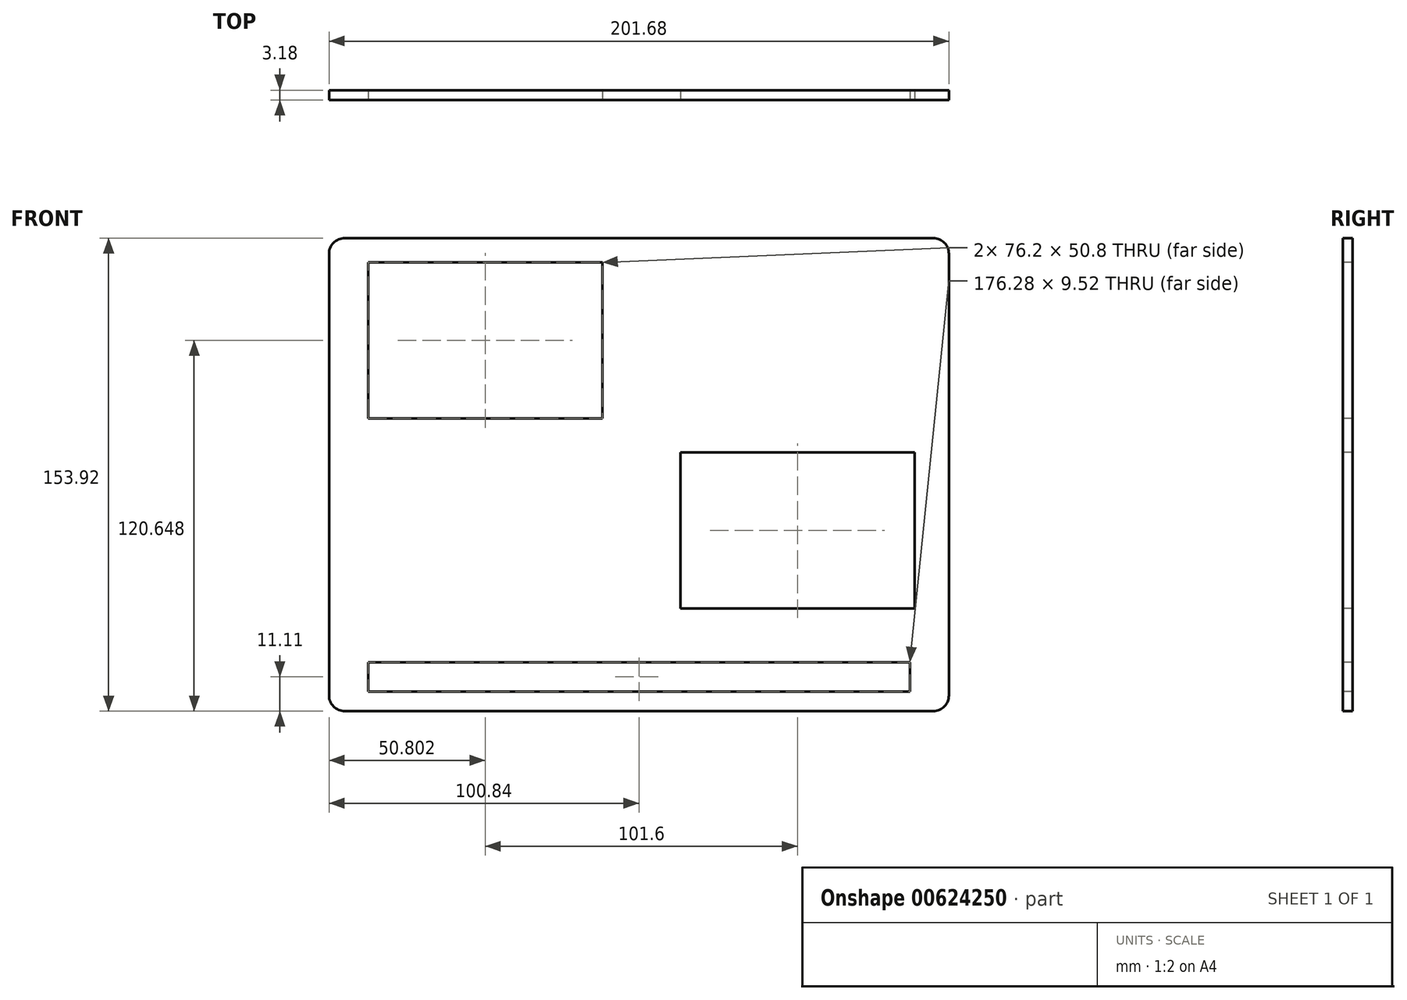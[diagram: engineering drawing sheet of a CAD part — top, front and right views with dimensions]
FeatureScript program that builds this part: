
annotation { "Feature Type Name" : "Feature", "Feature Type Description" : "" }
export const myFeature = defineFeature(function(context is Context, id is Id, definition is map)
    precondition{}
    {
        {
            var Q0;
            Q0=qCreatedBy(makeId("Front.planeOp"),FACE);
            var sketch = newSketch(context, id + "F0", { "sketchPlane" : qUnion([Q0])});
            skLineSegment(sketch, "E0.bottom", {"start": v(-100.84, 76.96) * mm, "end": v(100.84, 76.96) * mm});
            skLineSegment(sketch, "E0.top", {"start": v(-100.84, -76.96) * mm, "end": v(100.84, -76.96) * mm});
            skLineSegment(sketch, "E0.left", {"start": v(-100.84, 76.96) * mm, "end": v(-100.84, -76.96) * mm});
            skLineSegment(sketch, "E0.right", {"start": v(100.84, 76.96) * mm, "end": v(100.84, -76.96) * mm});
            skPoint(sketch, "E0.middle", {"position": v(0, 0) * mm});
            skSolve(sketch);
        }
        {
            var Q0;
            Q0=qSketchRegion(id+"F0",true);
            extrude(context, id + "F1", {"entities" : qUnion([Q0]), "depth" : 3.17 * mm, "offsetDistance" : 25.4 * mm});
        }
        {
            var Q0;
            Q0=makeQuery(id+"F1.opExtrude","CAP_FACE",FACE,{"disambiguationData":[OSD([sQuery(id+"F0.wireOp",EDGE,"E0.bottom"),sQuery(id+"F0.wireOp",EDGE,"E0.top"),sQuery(id+"F0.wireOp",EDGE,"E0.left"),sQuery(id+"F0.wireOp",EDGE,"E0.right")])],"isStart":false});
            var sketch = newSketch(context, id + "F2", { "sketchPlane" : qUnion([Q0])});
            skLineSegment(sketch, "E1.bottom", {"start": v(-88.14, 69.09) * mm, "end": v(-11.94, 69.09) * mm});
            skLineSegment(sketch, "E1.top", {"start": v(-88.14, 18.29) * mm, "end": v(-11.94, 18.29) * mm});
            skLineSegment(sketch, "E1.left", {"start": v(-88.14, 69.09) * mm, "end": v(-88.14, 18.29) * mm});
            skLineSegment(sketch, "E1.right", {"start": v(-11.94, 69.09) * mm, "end": v(-11.94, 18.29) * mm});
            skLineSegment(sketch, "E2.bottom", {"start": v(13.46, 7.18) * mm, "end": v(89.66, 7.18) * mm});
            skLineSegment(sketch, "E2.top", {"start": v(13.46, -43.62) * mm, "end": v(89.66, -43.62) * mm});
            skLineSegment(sketch, "E2.left", {"start": v(13.46, 7.18) * mm, "end": v(13.46, -43.62) * mm});
            skLineSegment(sketch, "E2.right", {"start": v(89.66, 7.18) * mm, "end": v(89.66, -43.62) * mm});
            skSolve(sketch);
        }
        {
            var Q0;
            Q0=qSketchRegion(id+"F2",true);
            extrude(context, id + "F3", {"entities" : qUnion([Q0]), "operationType" : NewBodyOperationType.REMOVE, "endBound" : BoundingType.THROUGH_ALL, "oppositeDirection" : true, "depth" : 25.4 * mm, "offsetDistance" : 25.4 * mm});
        }
        {
            var Q0;
            Q0=makeQuery(id+"F1.opExtrude","CAP_FACE",FACE,{"disambiguationData":[OSD([sQuery(id+"F0.wireOp",EDGE,"E0.bottom"),sQuery(id+"F0.wireOp",EDGE,"E0.top"),sQuery(id+"F0.wireOp",EDGE,"E0.left"),sQuery(id+"F0.wireOp",EDGE,"E0.right")])],"isStart":false});
            var sketch = newSketch(context, id + "F4", { "sketchPlane" : qUnion([Q0])});
            skLineSegment(sketch, "E3.bottom", {"start": v(-88.14, -61.09) * mm, "end": v(88.14, -61.09) * mm});
            skLineSegment(sketch, "E3.top", {"start": v(-88.14, -70.61) * mm, "end": v(88.14, -70.61) * mm});
            skLineSegment(sketch, "E3.left", {"start": v(-88.14, -61.09) * mm, "end": v(-88.14, -70.61) * mm});
            skLineSegment(sketch, "E3.right", {"start": v(88.14, -61.09) * mm, "end": v(88.14, -70.61) * mm});
            skSolve(sketch);
        }
        {
            var Q0;
            Q0=qSketchRegion(id+"F4",true);
            extrude(context, id + "F5", {"entities" : qUnion([Q0]), "operationType" : NewBodyOperationType.REMOVE, "endBound" : BoundingType.THROUGH_ALL, "oppositeDirection" : true, "depth" : 25.4 * mm, "offsetDistance" : 25.4 * mm});
        }
        {
            var Q0;
            Q0=makeQuery(id+"F1.opExtrude","SWEPT_EDGE",EDGE,{"disambiguationData":[OSD([sQuery(id+"F0.wireOp",EDGE,"E0.bottom"),sQuery(id+"F0.wireOp",EDGE,"E0.right")])]});
            var Q1;
            Q1=makeQuery(id+"F1.opExtrude","SWEPT_EDGE",EDGE,{"disambiguationData":[OSD([sQuery(id+"F0.wireOp",EDGE,"E0.top"),sQuery(id+"F0.wireOp",EDGE,"E0.right")])]});
            var Q2;
            Q2=makeQuery(id+"F1.opExtrude","SWEPT_EDGE",EDGE,{"disambiguationData":[OSD([sQuery(id+"F0.wireOp",EDGE,"E0.bottom"),sQuery(id+"F0.wireOp",EDGE,"E0.left")])]});
            var Q3;
            Q3=makeQuery(id+"F1.opExtrude","SWEPT_EDGE",EDGE,{"disambiguationData":[OSD([sQuery(id+"F0.wireOp",EDGE,"E0.top"),sQuery(id+"F0.wireOp",EDGE,"E0.left")])]});
            fillet(context, id + "F6", {"entities" : qUnion([Q0, Q1, Q2, Q3]), "radius" : 5.08 * mm, "tangentPropagation" : true, "allowEdgeOverflow" : false});
        }
    });
